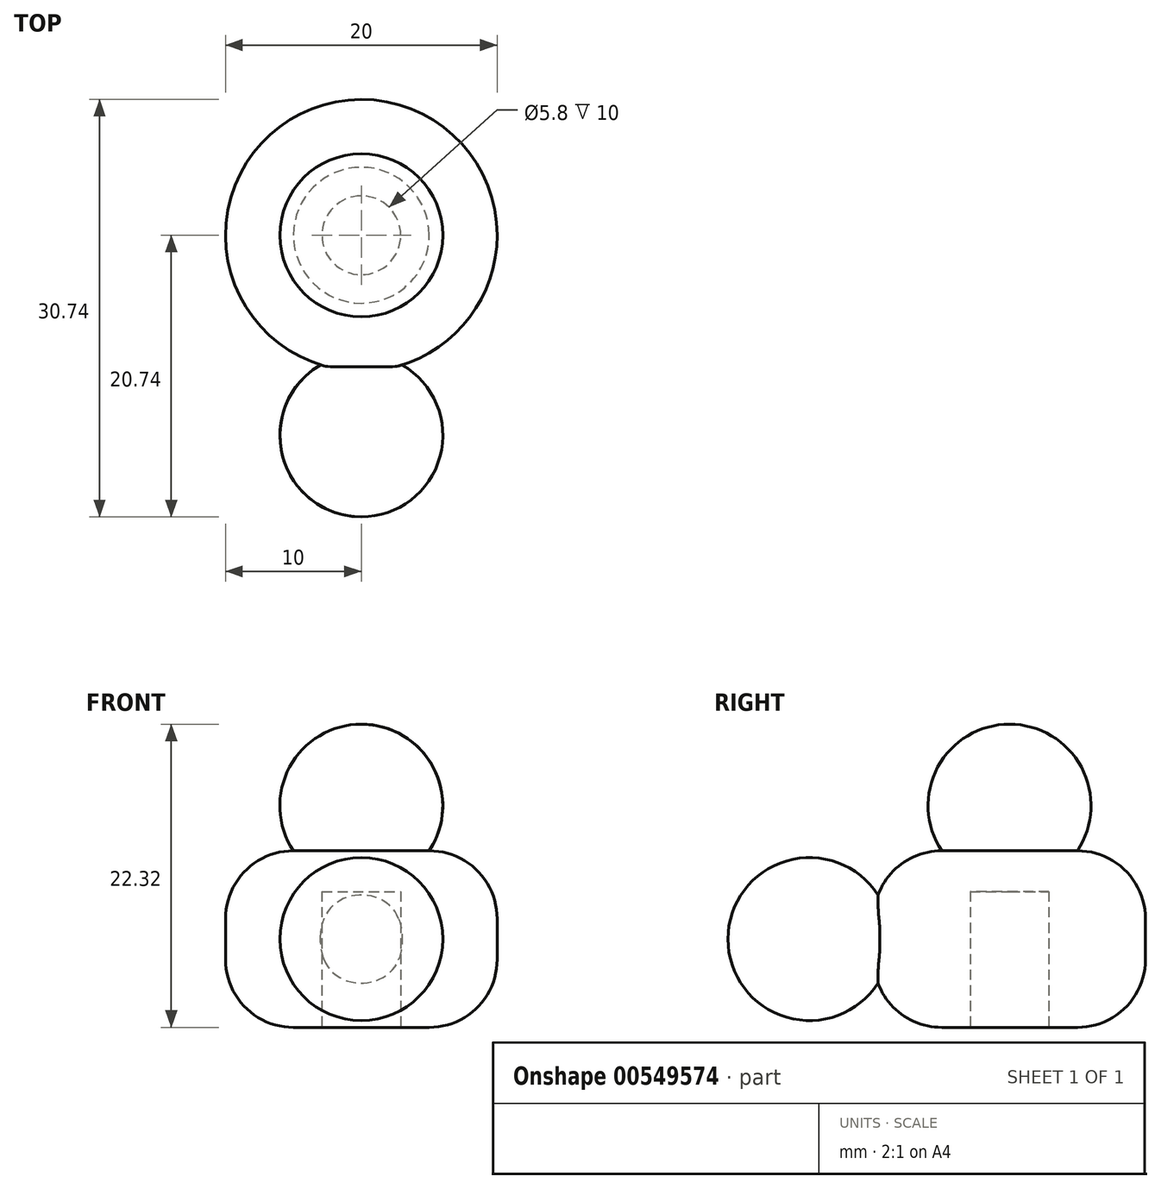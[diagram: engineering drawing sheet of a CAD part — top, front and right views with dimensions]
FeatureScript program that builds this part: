
annotation { "Feature Type Name" : "Feature", "Feature Type Description" : "" }
export const myFeature = defineFeature(function(context is Context, id is Id, definition is map)
    precondition{}
    {
        {
            var Q0;
            Q0=qCreatedBy(makeId("Top.planeOp"),FACE);
            var sketch = newSketch(context, id + "F0", { "sketchPlane" : qUnion([Q0])});
            skCircle(sketch, "E0", {"center": v(0, 0) * mm, "radius": 10 * mm});
            skSolve(sketch);
        }
        {
            var Q0;
            Q0=qSketchRegion(id+"F0",true);
            extrude(context, id + "F1", {"entities" : qUnion([Q0]), "endBound" : BoundingType.SYMMETRIC, "depth" : 13 * mm, "offsetDistance" : 25 * mm});
        }
        {
            var Q0;
            Q0=makeQuery(id+"F1.opExtrude","CAP_FACE",FACE,{"disambiguationData":[OSD([sQuery(id+"F0.wireOp",EDGE,"E0")])],"isStart":true});
            var sketch = newSketch(context, id + "F2", { "sketchPlane" : qUnion([Q0])});
            skCircle(sketch, "E1", {"center": v(0, 0) * mm, "radius": 2.9 * mm});
            skSolve(sketch);
        }
        {
            var Q0;
            Q0=qSketchRegion(id+"F2",true);
            extrude(context, id + "F3", {"entities" : qUnion([Q0]), "operationType" : NewBodyOperationType.REMOVE, "oppositeDirection" : true, "depth" : 10 * mm, "offsetDistance" : 25 * mm});
        }
        {
            var Q0;
            Q0=qCreatedBy(makeId("Top.planeOp"),FACE);
            var sketch = newSketch(context, id + "F4", { "sketchPlane" : qUnion([Q0])});
            skLineSegment(sketch, "E2", {"start": v(0, 0) * mm, "end": v(0, -46.52) * mm, "construction": true});
            skLineSegment(sketch, "E3", {"start": v(0, -9.54) * mm, "end": v(-3, -9.54) * mm});
            skLineSegment(sketch, "E4", {"start": v(-3, -9.54) * mm, "end": v(-3, -9.54) * mm});
            skArc(sketch, "E5", {"start": v(-3, -9.54) * mm, "mid": v(-5.8, -16.29) * mm, "end": v(0, -20.74) * mm});
            skLineSegment(sketch, "E6", {"start": v(0, -9.54) * mm, "end": v(0, -20.74) * mm});
            skSolve(sketch);
        }
        {
            var Q0;
            Q0=qSketchRegion(id+"F4",true);
            var Q1;
            Q1=sQuery(id+"F4.wireOp",EDGE,"E2");
            revolve(context, id + "F5", {"operationType" : NewBodyOperationType.ADD, "entities" : qUnion([Q0]), "axis" : qUnion([Q1]), "revolveType" : RevolveType.FULL});
        }
        {
            var Q0;
            Q0=makeQuery(id+"F1.opExtrude","CAP_EDGE",EDGE,{"disambiguationData":[OSD([sQuery(id+"F0.wireOp",EDGE,"E0")])],"isStart":true});
            var Q1;
            Q1=makeQuery(id+"F1.opExtrude","CAP_EDGE",EDGE,{"disambiguationData":[OSD([sQuery(id+"F0.wireOp",EDGE,"E0")])],"isStart":false});
            fillet(context, id + "F6", {"entities" : qUnion([Q0, Q1]), "radius" : 5 * mm, "tangentPropagation" : true, "allowEdgeOverflow" : false});
        }
        {
            var Q0;
            Q0=qCreatedBy(makeId("Front.planeOp"),FACE);
            var sketch = newSketch(context, id + "F7", { "sketchPlane" : qUnion([Q0])});
            skArc(sketch, "E7", {"start": v(0, 15.82) * mm, "mid": v(5.77, 11.44) * mm, "end": v(3.13, 4.7) * mm});
            skLineSegment(sketch, "E8", {"start": v(3.13, 4.7) * mm, "end": v(0, 6.5) * mm});
            skLineSegment(sketch, "E9", {"start": v(0, 15.82) * mm, "end": v(0, 6.5) * mm});
            skLineSegment(sketch, "E10", {"start": v(0, 0) * mm, "end": v(0, 20.08) * mm, "construction": true});
            skLineSegment(sketch, "E11.0.0", {"start": v(-5, 6.5) * mm, "end": v(5, 6.5) * mm, "construction": true});
            skSolve(sketch);
        }
        {
            var Q0;
            Q0 = qSketchRegion(id + "F7", true);
            var Q1;
            Q1=sQuery(id+"F7.wireOp",EDGE,"E10");
            revolve(context, id + "F8", {"operationType" : NewBodyOperationType.ADD, "entities" : qUnion([Q0]), "axis" : qUnion([Q1]), "revolveType" : RevolveType.FULL});
        }
    });
